# Revit family: G7X MS440507PM
name_source: partatom
category: Datengeräte
units: mm (PartAtom-declared; Revit-internal decimal feet)

## family parameters
Arbeitsebenenbasiert = Nein
Beim Laden mit Abzugskörper schneiden = Nein
Bemaßung runder Anschluss = Durchmesser verwenden
Beschriftungsausrichtung beibehalten = Nein
Gemeinsam genutzt = Nein
Immer vertikal = Ja
OmniClass-Nummer = 23.85.50.17
OmniClass-Titel = Communication and Data Processing Equipment
Raumberechnungspunkt = Nein
Teiletyp = Normal

## types (1)
- G7X MS440507PM
    Artikelnummer = MS440507PM
    Beschreibung = 7-Port 10G Micro Switch PoE++
    Hersteller = MICROSENS
    Interface 1 = 2x 1/10GBase-X SFP+ Slots
    Interface 2 = 4x 10/100/1000T PoE+
    Interface 3 = 1x 1/2.5/5GBase-T, PoE++
    Interface 4 = Console port (USB C)
    Property 1 = M45 Design
    Property 2 = managed switch
    Type = horizontal
    Voltage = 22..57 VDC
    Vorgabe-Ansicht = 0 mm  [stored 0 ft]

note: [stored X ft] marks values corroborated as IEEE doubles in the binary element streams (Revit-internal decimal feet)
